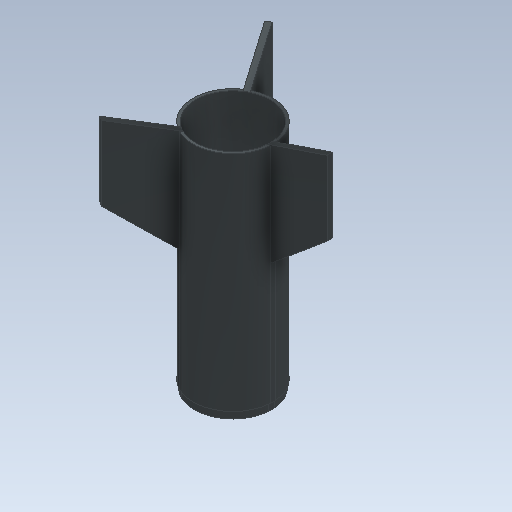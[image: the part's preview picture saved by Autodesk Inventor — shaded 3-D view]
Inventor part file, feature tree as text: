
AUTODESK INVENTOR PART (.ipt)
format: ipt  version: 2020.3 (Build 243373000, 373)  size: 205,312 bytes
history: native  units: mm
features: extrude x3, sketch x2, projected_geometry x2, pattern_circular x1
ambient origin geometry x8: Origin, YZ Plane, XZ Plane, XY Plane, X Axis, Y Axis, Z Axis, Center Point
bodies: Solid1 (feature_tree)
feature tree (8):
  sketch  "Sketch1"  dims[d0=50.0mm d1=51.8mm]
  extrude  "Extrusion1"  Depth=51.8mm
  extrude  "Extrusion2"  Depth=75.0mm TaperAngle=0.0deg
  extrude  "Extrusion4"  Depth=75.0mm TaperAngle=0.0deg
  pattern_circular  "Circular Pattern2"  Count=7  [1 undecoded]
  sketch  "Sketch4"  dims[d2=53.6mm d3=75.0mm d4=80.0mm d5=0.0mm d6=0.0mm d7=75.0mm d8=0.0mm d18=70.0mm d21=8.726646mm d24=50.0mm d25=40.0mm d26=3.6mm d27=0.0mm d28=30.0mm d29=360.0deg d31=75.0mm d32=0.0mm d11=0.5mm d12=0.872665mm d13=0.5mm d14=0.872665mm d33=0.5mm d34=0.872665mm]
  projected_geometry  "Projected Loop1"
  projected_geometry  "Project Cut Edges1"
note: 1 required parameter value undecoded (feature->parameter linkage not recoverable at this tier; creation-order binding heuristic only, values carry confidence <= 0.55)
